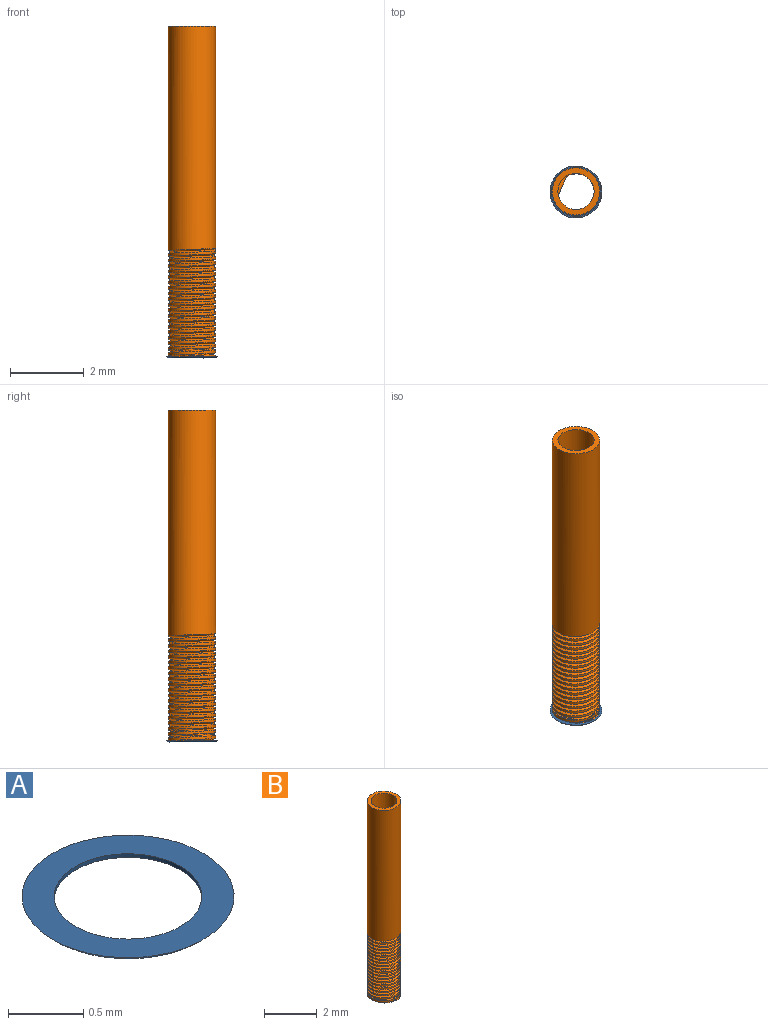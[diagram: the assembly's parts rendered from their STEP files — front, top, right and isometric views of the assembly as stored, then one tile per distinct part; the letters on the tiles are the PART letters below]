
ASSEMBLY  parts=2 mates=1
PART A: 4 faces, bbox 1.4x1.4x0 mm
  f0: cylinder r=0.49mm len=0.99mm, axis (0,0,-1), area 0.1mm2, adj f1,f2
  f1: plane 1.41x1.41mm, normal (0,0,1), area 0.8mm2, adj f0,f3
  f2: plane 1.35x1.35mm, normal (0,0,-1), area 0.7mm2, adj f0,f3
  f3: cone r=0.71mm half-angle=45deg, axis (0,0,1), area 0.2mm2, adj f1,f2
PART B: 27 faces, bbox 1.3x1.5x9.1 mm
  f0: cylinder r=0.49mm len=9mm, axis (0,0,-1), area 27.9mm2, adj f22,f23
  f1: cylinder r=0.64mm len=6.19mm, axis (0,0,-1), area 24.7mm2, adj f2,f22,f24,f26
  f2: cylinder r=0.64mm len=1.29mm, axis (0,0,-1), area 0.3mm2, adj f1,f3,f24,f25
  f3: cylinder r=0.64mm len=1.29mm, axis (0,0,-1), area 0.3mm2, adj f2,f4,f24,f25
  f4: cylinder r=0.64mm len=1.29mm, axis (0,0,-1), area 0.3mm2, adj f3,f5,f24,f25
  f5: cylinder r=0.64mm len=1.29mm, axis (0,0,-1), area 0.3mm2, adj f4,f6,f24,f25
  f6: cylinder r=0.64mm len=1.29mm, axis (0,0,-1), area 0.3mm2, adj f5,f7,f24,f25
  f7: cylinder r=0.64mm len=1.29mm, axis (0,0,-1), area 0.3mm2, adj f6,f8,f24,f25
  f8: cylinder r=0.64mm len=1.29mm, axis (0,0,-1), area 0.3mm2, adj f7,f9,f24,f25
  f9: cylinder r=0.64mm len=1.29mm, axis (0,0,-1), area 0.3mm2, adj f8,f10,f24,f25
  f10: cylinder r=0.64mm len=1.29mm, axis (0,0,-1), area 0.3mm2, adj f9,f11,f24,f25
  f11: cylinder r=0.64mm len=1.29mm, axis (0,0,-1), area 0.3mm2, adj f10,f12,f24,f25
  f12: cylinder r=0.64mm len=1.29mm, axis (0,0,-1), area 0.3mm2, adj f11,f13,f24,f25
  f13: cylinder r=0.64mm len=1.29mm, axis (0,0,-1), area 0.3mm2, adj f12,f14,f24,f25
  f14: cylinder r=0.64mm len=1.29mm, axis (0,0,-1), area 0.3mm2, adj f13,f15,f24,f25
  f15: cylinder r=0.64mm len=1.29mm, axis (0,0,-1), area 0.3mm2, adj f14,f16,f24,f25
  f16: cylinder r=0.64mm len=1.29mm, axis (0,0,-1), area 0.3mm2, adj f15,f17,f24,f25
  f17: cylinder r=0.64mm len=1.29mm, axis (0,0,-1), area 0.3mm2, adj f16,f18,f24,f25
  f18: cylinder r=0.64mm len=1.29mm, axis (0,0,-1), area 0.3mm2, adj f17,f19,f24,f25
  f19: cylinder r=0.64mm len=1.29mm, axis (0,0,-1), area 0.3mm2, adj f18,f20,f24,f25
  f20: cylinder r=0.64mm len=1.29mm, axis (0,0,-1), area 0.3mm2, adj f19,f21,f23,f24,f25
  f21: cylinder r=0.64mm len=0.61mm, axis (0,0,-1), area 0mm2, adj f20,f23,f25
  f22: plane 1.29x1.29mm, normal (0,0,1), area 0.5mm2, adj f0,f1
  f23: plane 1.31x1.26mm, normal (0,0,-1), area 0.5mm2, adj f0,f20,f21,f24,f25
  f24: bspline ~3.02x1.48mm, area 6mm2, adj f1,f2,f3,f4,f5,f6,f7,f8
  f25: bspline ~2.96x1.29mm, area 5.9mm2, adj f2,f3,f4,f5,f6,f7,f8,f9
  f26: plane 0.08x0.07mm, normal (0,-1,0), area 0mm2, adj f1,f24,f25
PLACE A rot(axis=(-0.8,0.37,-0.47),0deg) t=(-3.46,0.41,-0.41)mm
PLACE B rot(axis=(-0.8,0.37,-0.47),0deg) t=(-3.46,0.41,-0.38)mm
MATE planar A.f0 <-> B.f0  axis (0,0,1) through (-3.46,0.41,-0.38)mm
